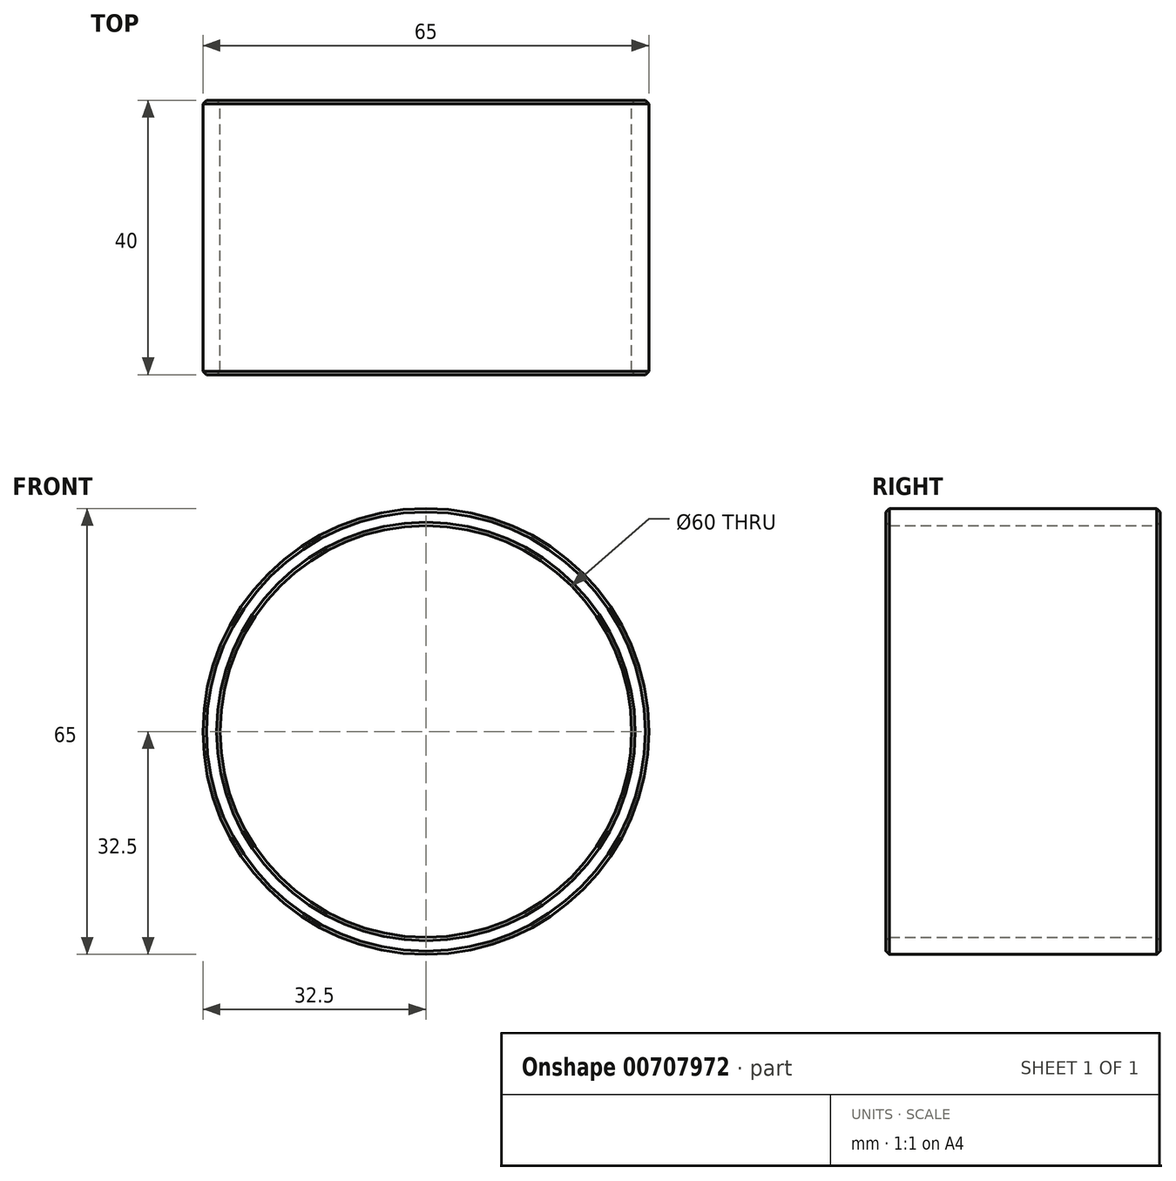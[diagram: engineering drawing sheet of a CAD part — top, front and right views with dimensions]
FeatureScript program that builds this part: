
annotation { "Feature Type Name" : "Feature", "Feature Type Description" : "" }
export const myFeature = defineFeature(function(context is Context, id is Id, definition is map)
    precondition{}
    {
        {
            var Q0;
            Q0=qCreatedBy(makeId("Front.planeOp"),FACE);
            var sketch = newSketch(context, id + "F0", { "sketchPlane" : qUnion([Q0])});
            skCircle(sketch, "E0", {"center": v(0, 0) * mm, "radius": 32.5 * mm});
            skCircle(sketch, "E1", {"center": v(0, 0) * mm, "radius": 30 * mm});
            skSolve(sketch);
        }
        {
            var Q0;
            Q0=makeQuery(id+"F0.imprint","IMPRINT",FACE,{"disambiguationData":[TD([[makeQuery(id+"F0.imprint","IMPRINT",EDGE,{"derivedFrom":sQuery(id+"F0.wireOp",EDGE,"E0")}),1.0]])]});
            extrude(context, id + "F1", {"entities" : qUnion([Q0]), "endBound" : BoundingType.SYMMETRIC, "depth" : 40 * mm, "offsetDistance" : 25 * mm});
        }
        {
            var Q0;
            Q0=makeQuery(id+"F1.opExtrude","SWEPT_FACE",FACE,{"disambiguationData":[OSD([sQuery(id+"F0.wireOp",EDGE,"E1")])]});
            var Q1;
            Q1=makeQuery(id+"F1.opExtrude","SWEPT_FACE",FACE,{"disambiguationData":[OSD([sQuery(id+"F0.wireOp",EDGE,"E0")])]});
            chamfer(context, id + "F2", {"entities" : qUnion([Q0, Q1]), "width" : 0.5 * mm, "tangentPropagation" : true});
        }
    });
